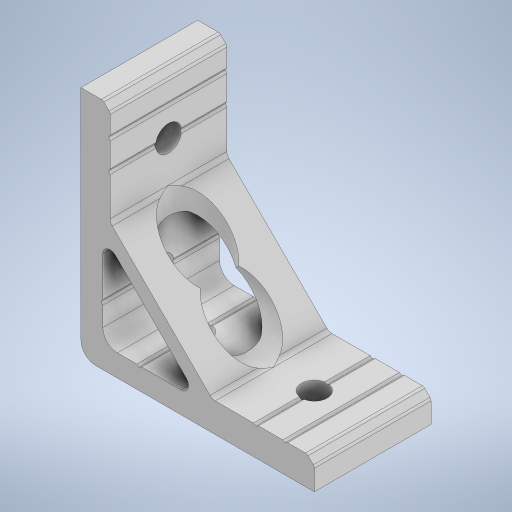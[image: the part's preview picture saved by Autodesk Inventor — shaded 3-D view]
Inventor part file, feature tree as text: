
AUTODESK INVENTOR PART (.ipt)
format: ipt  version: 2023 (Build 270158000, 158)  size: 312,832 bytes
history: native  units: in
note: dims shown in document units (in); Inventor stores cm internally (conversion verified against a paired STEP export)
features: fillet x1
ambient origin geometry x8: Origin, YZ Plane, XZ Plane, XY Plane, X Axis, Y Axis, Z Axis, Center Point
bodies: Solid1 (feature_tree)
feature tree (1):
  fillet  "Fillet6"  [1 undecoded]
note: 1 required parameter value undecoded (feature->parameter linkage not recoverable at this tier; creation-order binding heuristic only, values carry confidence <= 0.55)
